# Revit family: Robe_Hook-DXV-Oak_Hill-D35155210_Series
name_source: partatom
category: Specialty Equipment
units: mm (PartAtom-declared; Revit-internal decimal feet)

## family parameters
Cut with Voids When Loaded = No
Host = Face
OmniClass Number = 23.40.20.21.31
OmniClass Title = Robe Hooks
Part Type = Normal
Room Calculation Point = No
Round Connector Dimension = Use Diameter
Shared = Yes

## types (4) — shared parameters
Assembly Code = C1030220
Base Diameter = 2"
Base Radius = 1"
Default Elevation = 48"
Description = Robe Hook
Height = 3 1/8"
Installation Type = Wall Mount
Length = 2 7/16"
Manufacturer = DXV
Price = Prices may vary. Please consult Manufacturer Representative for most up-to-date price list.
URL = https://www.dxv.com
Width = 3 7/8"

## per-type parameters (varying)
| type | Finish | Material |
| D35155210.100 | Metal-DXV-100-Polished Chrome | Metal-DXV-100-Polished Chrome |
| D35155210.144 | Metal-DXV-144-Brushed Nickel | Metal-DXV-144-Brushed Nickel |
| D35155210.150 | Metal-DXV-150-Platinum Nickel | Metal-DXV-150-Platinum Nickel |
| D35155210.427 | Metal-DXV-427-Satin Brass | Metal-DXV-427-Satin Brass |

note: column(s) folded — value = type name in every type: Model

## geometry (parser evidence)
native form markers: Sweep x3
no freeform markers — native parametric forms only
